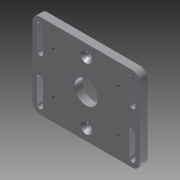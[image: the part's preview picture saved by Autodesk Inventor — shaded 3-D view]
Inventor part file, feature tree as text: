
AUTODESK INVENTOR PART (.ipt)
format: ipt  version: 2012 (Build 160160000, 160)  size: 145,408 bytes
history: native  units: in
note: dims shown in document units (in); Inventor stores cm internally (conversion verified against a paired STEP export)
features: extrude x2, hole x2, sketch x1, fillet x1
ambient origin geometry x8: Origin, YZ Plane, XZ Plane, XY Plane, X Axis, Y Axis, Z Axis, Center Point
bodies: Solid1 (feature_tree)
feature tree (6):
  sketch  "Sketch1"  dims[d0=2.75in d1=0.75in d2=1.0in d3=1.0in d4=1.055in d5=0.6875in d6=0.6875in d7=1.055in d8=0.25in d9=0.0in d10=0.104in d11=0.75in d12=0.375in d13=0.25in d14=0.5635in d15=1.0in d16=0.8108in d17=0.19in d18=0.339in d19=0.375in d20=0.25in d21=0.5635in d22=1.0in d23=0.8108in d24=1.375in d25=2.75in d26=1.75in d28=1.75in d30=0.2in d31=0.75in d33=0.25in d34=0.25in d35=0.7874in d37=3.0in d38=0.7874in d40=1.5in d43=0.25in d44=0.0in d45=0.25in]
  extrude  "Extrusion1"  Depth=0.75in
  hole  "Hole1"  [1 undecoded]
  hole  "Hole2"  [1 undecoded]
  extrude  "Extrusion2"  Depth=1.055in
  fillet  "Fillet1"  Radius=0.6875in
note: 2 required parameter values undecoded (feature->parameter linkage not recoverable at this tier; creation-order binding heuristic only, values carry confidence <= 0.55)
